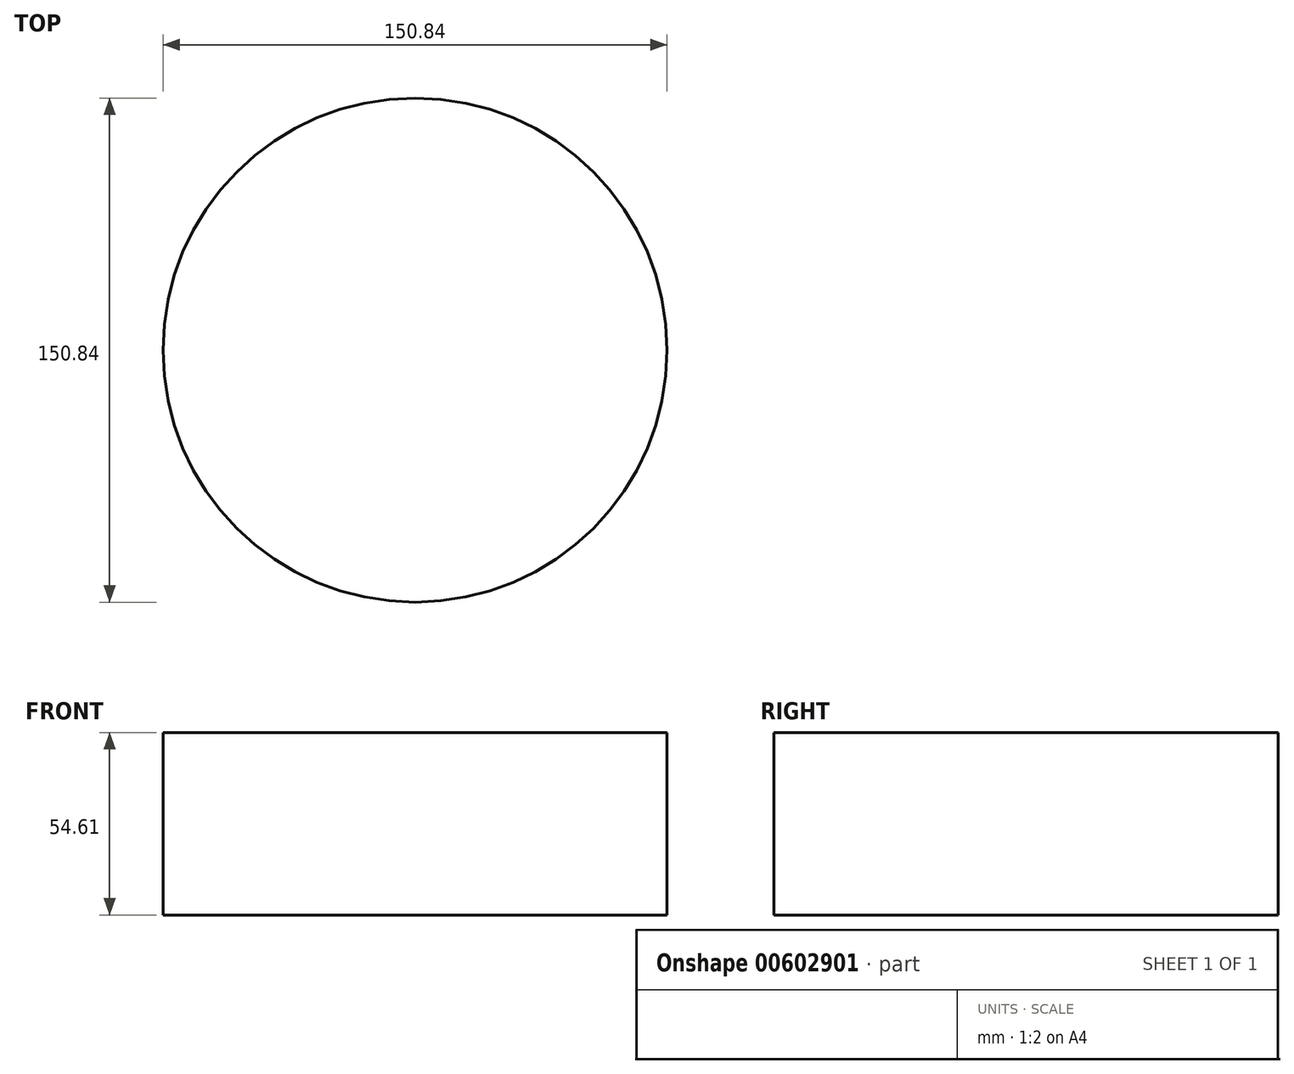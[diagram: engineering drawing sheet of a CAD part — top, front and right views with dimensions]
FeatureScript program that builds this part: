
annotation { "Feature Type Name" : "Feature", "Feature Type Description" : "" }
export const myFeature = defineFeature(function(context is Context, id is Id, definition is map)
    precondition{}
    {
        {
            var Q0;
            Q0=qCreatedBy(makeId("Top.planeOp"),FACE);
            var sketch = newSketch(context, id + "F0", { "sketchPlane" : qUnion([Q0])});
            skCircle(sketch, "E0", {"center": v(0, 0) * mm, "radius": 75.42 * mm});
            skSolve(sketch);
        }
        {
            var Q0;
            Q0=makeQuery(id+"F0.imprint","IMPRINT",FACE,{"disambiguationData":[TD([[makeQuery(id+"F0.imprint","IMPRINT",EDGE,{"derivedFrom":sQuery(id+"F0.wireOp",EDGE,"E0")}),1.0]])]});
            extrude(context, id + "F1", {"entities" : qUnion([Q0]), "depth" : 54.6 * mm, "offsetDistance" : 25.4 * mm});
        }
    });
